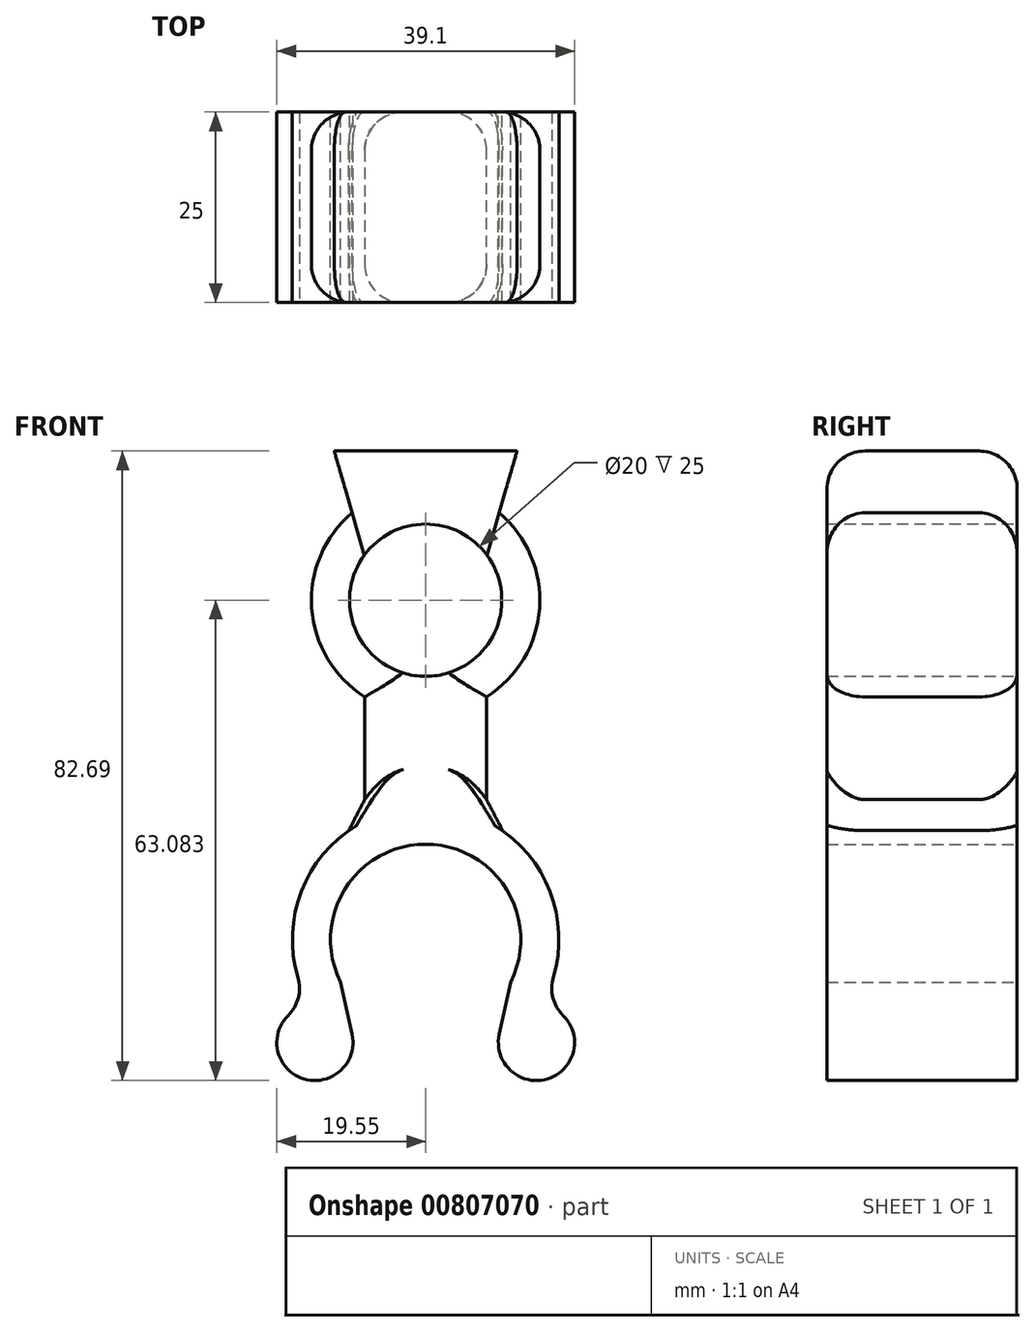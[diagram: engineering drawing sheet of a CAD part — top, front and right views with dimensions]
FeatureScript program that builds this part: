
annotation { "Feature Type Name" : "Feature", "Feature Type Description" : "" }
export const myFeature = defineFeature(function(context is Context, id is Id, definition is map)
    precondition{}
    {
        {
            var Q0;
            Q0=qCreatedBy(makeId("Front.planeOp"),FACE);
            var sketch = newSketch(context, id + "F0", { "sketchPlane" : qUnion([Q0])});
            skArc(sketch, "E0", {"start": v(15.25, -8.59) * mm, "mid": v(16.76, 5.03) * mm, "end": v(8, 15.56) * mm});
            skArc(sketch, "E1", {"start": v(11.16, -5.63) * mm, "mid": v(10.65, 6.55) * mm, "end": v(0, 12.5) * mm});
            skLineSegment(sketch, "E2", {"start": v(0, 17.5) * mm, "end": v(0, 12.5) * mm});
            skLineSegment(sketch, "E3", {"start": v(11.16, -5.63) * mm, "end": v(9.67, -12.47) * mm});
            skArc(sketch, "E4", {"start": v(9.67, -12.47) * mm, "mid": v(17.4, -17.64) * mm, "end": v(15.25, -8.59) * mm});
            skArc(sketch, "E5", {"start": v(0, 34.54) * mm, "mid": v(10, 44.54) * mm, "end": v(0, 54.54) * mm});
            skArc(sketch, "E6", {"start": v(8, 31.85) * mm, "mid": v(14.96, 43.52) * mm, "end": v(9.66, 56.02) * mm});
            skLineSegment(sketch, "E7", {"start": v(0, 59.54) * mm, "end": v(0, 69.88) * mm});
            skLineSegment(sketch, "E8", {"start": v(0, -9.02) * mm, "end": v(0, 85.69) * mm, "construction": true});
            skLineSegment(sketch, "E9", {"start": v(0, 59.54) * mm, "end": v(0, 54.54) * mm});
            skLineSegment(sketch, "E10", {"start": v(0, 29.54) * mm, "end": v(0, 34.54) * mm});
            skLineSegment(sketch, "E11", {"start": v(8, 31.85) * mm, "end": v(8, 15.56) * mm});
            skLineSegment(sketch, "E12", {"start": v(0, 29.54) * mm, "end": v(0, 17.5) * mm});
            skLineSegment(sketch, "E13", {"start": v(12, 64.15) * mm, "end": v(0, 64.15) * mm});
            skLineSegment(sketch, "E14", {"start": v(12, 64.15) * mm, "end": v(9.66, 56.02) * mm});
            skSolve(sketch);
        }
        {
            var Q0;
            Q0=qSketchRegion(id+"F0",true);
            extrude(context, id + "F1", {"entities" : qUnion([Q0]), "depth" : 25 * mm, "offsetDistance" : 25 * mm});
        }
        {
            var Q0;
            Q0=makeQuery(id+"F1.opExtrude","SWEPT_BODY",BODY,{"disambiguationData":[OSD([sQuery(id+"F0.wireOp",EDGE,"E0"),sQuery(id+"F0.wireOp",EDGE,"E1"),sQuery(id+"F0.wireOp",EDGE,"E2"),sQuery(id+"F0.wireOp",EDGE,"E3"),sQuery(id+"F0.wireOp",EDGE,"E4")])]});
            var Q1;
            Q1=makeQuery(id+"F1.opExtrude","SWEPT_BODY",BODY,{"disambiguationData":[OSD([sQuery(id+"F0.wireOp",EDGE,"E5"),sQuery(id+"F0.wireOp",EDGE,"E6"),sQuery(id+"F0.wireOp",EDGE,"ZKlF4mqJ-5DrE-eTdW-whtT-mimaQSIe7lm9"),sQuery(id+"F0.wireOp",EDGE,"B9OKSv2O-DWHs-XMQp-p7Ia-sCPH9sulsA8u"),sQuery(id+"F0.wireOp",EDGE,"7JTtOB6v-8xqh-fVU6-w0FL-nSfP0XwtOn2y"),sQuery(id+"F0.wireOp",EDGE,"698f7dfc-63ae-4ce6-86f1-02b924555ac6.filletArc"),sQuery(id+"F0.wireOp",EDGE,"46WvWRZJ-fj3N-dYTW-aIvH-BbHphLMpPgnm"),sQuery(id+"F0.wireOp",EDGE,"E9"),sQuery(id+"F0.wireOp",EDGE,"E10")])]});
            var Q2;
            Q2=qCreatedBy(makeId("Right.planeOp"),FACE);
            mirror(context, id + "F2", {"operationType" : NewBodyOperationType.ADD, "entities" : qUnion([Q0, Q1]), "mirrorPlane" : qUnion([Q2])});
        }
        {
            var Q0;
            Q0=makeQuery(id+"F2.opPattern","COPY",EDGE,{"derivedFrom":makeQuery(id+"F1.opExtrude","CAP_EDGE",EDGE,{"disambiguationData":[OSD([sQuery(id+"F0.wireOp",EDGE,"E6")])],"isStart":false}),"instanceName":"1"});
            var Q1;
            Q1=makeQuery(id+"F1.opExtrude","CAP_EDGE",EDGE,{"disambiguationData":[OSD([sQuery(id+"F0.wireOp",EDGE,"E6")])],"isStart":false});
            var Q2;
            Q2=makeQuery(id+"F1.opExtrude","CAP_EDGE",EDGE,{"disambiguationData":[OSD([sQuery(id+"F0.wireOp",EDGE,"E6")])],"isStart":true});
            var Q3;
            Q3=makeQuery(id+"F2.opPattern","COPY",EDGE,{"derivedFrom":makeQuery(id+"F1.opExtrude","CAP_EDGE",EDGE,{"disambiguationData":[OSD([sQuery(id+"F0.wireOp",EDGE,"E6")])],"isStart":true}),"instanceName":"1"});
            var Q4;
            Q4=makeQuery(id+"F1.opExtrude","CAP_EDGE",EDGE,{"disambiguationData":[OSD([sQuery(id+"F0.wireOp",EDGE,"E11")])],"isStart":true});
            var Q5;
            Q5=makeQuery(id+"F2.opPattern","COPY",EDGE,{"derivedFrom":makeQuery(id+"F1.opExtrude","CAP_EDGE",EDGE,{"disambiguationData":[OSD([sQuery(id+"F0.wireOp",EDGE,"E11")])],"isStart":true}),"instanceName":"1"});
            var Q6;
            Q6=makeQuery(id+"F2.opPattern","COPY",EDGE,{"derivedFrom":makeQuery(id+"F1.opExtrude","CAP_EDGE",EDGE,{"disambiguationData":[OSD([sQuery(id+"F0.wireOp",EDGE,"E11")])],"isStart":false}),"instanceName":"1"});
            var Q7;
            Q7=makeQuery(id+"F1.opExtrude","CAP_EDGE",EDGE,{"disambiguationData":[OSD([sQuery(id+"F0.wireOp",EDGE,"E11")])],"isStart":false});
            var Q8;
            Q8=makeQuery(id+"F2.opPattern","COPY",EDGE,{"derivedFrom":makeQuery(id+"F1.opExtrude","SWEPT_EDGE",EDGE,{"disambiguationData":[OSD([sQuery(id+"F0.wireOp",EDGE,"E0"),sQuery(id+"F0.wireOp",EDGE,"E4")])]}),"instanceName":"1"});
            var Q9;
            Q9=makeQuery(id+"F1.opExtrude","SWEPT_EDGE",EDGE,{"disambiguationData":[OSD([sQuery(id+"F0.wireOp",EDGE,"E0"),sQuery(id+"F0.wireOp",EDGE,"E4")])]});
            var Q10;
            {var subQ0=makeQuery(id+"F1.opExtrude","CAP_EDGE",EDGE,{"disambiguationData":[OSD([sQuery(id+"F0.wireOp",EDGE,"E13")])],"isStart":false});Q10=makeQuery(id+"F2.boolean.opBoolean","MERGE",EDGE,{"derivedFrom":[subQ0,makeQuery(id+"F2.opPattern","COPY",EDGE,{"derivedFrom":subQ0,"instanceName":"1"})]});}
            var Q11;
            {var subQ0=makeQuery(id+"F1.opExtrude","CAP_EDGE",EDGE,{"disambiguationData":[OSD([sQuery(id+"F0.wireOp",EDGE,"E13")])],"isStart":true});Q11=makeQuery(id+"F2.boolean.opBoolean","MERGE",EDGE,{"derivedFrom":[subQ0,makeQuery(id+"F2.opPattern","COPY",EDGE,{"derivedFrom":subQ0,"instanceName":"1"})]});}
            fillet(context, id + "F3", {"entities" : qUnion([Q0, Q1, Q2, Q3, Q4, Q5, Q6, Q7, Q8, Q9, Q10, Q11]), "radius" : 5 * mm, "tangentPropagation" : true, "allowEdgeOverflow" : false});
        }
        {
            var Q0;
            Q0=makeQuery(id+"F3.opFillet","BLEND_EDGE",EDGE,{"blendedFrom":[makeQuery(id+"F2.opPattern","COPY",EDGE,{"derivedFrom":makeQuery(id+"F1.opExtrude","CAP_EDGE",EDGE,{"disambiguationData":[OSD([sQuery(id+"F0.wireOp",EDGE,"E11")])],"isStart":false}),"instanceName":"1"}),makeQuery(id+"F2.opPattern","COPY",FACE,{"derivedFrom":makeQuery(id+"F1.opExtrude","SWEPT_FACE",FACE,{"disambiguationData":[OSD([sQuery(id+"F0.wireOp",EDGE,"E0")])]}),"instanceName":"1"})],"blendedInto":[makeQuery(id+"F2.opPattern","COPY",FACE,{"derivedFrom":makeQuery(id+"F1.opExtrude","SWEPT_FACE",FACE,{"disambiguationData":[OSD([sQuery(id+"F0.wireOp",EDGE,"E0")])]}),"instanceName":"1"})]});
            var Q1;
            Q1=makeQuery(id+"F3.opFillet","BLEND_EDGE",EDGE,{"blendedFrom":[makeQuery(id+"F1.opExtrude","CAP_EDGE",EDGE,{"disambiguationData":[OSD([sQuery(id+"F0.wireOp",EDGE,"E11")])],"isStart":false}),makeQuery(id+"F1.opExtrude","SWEPT_FACE",FACE,{"disambiguationData":[OSD([sQuery(id+"F0.wireOp",EDGE,"E0")])]})],"blendedInto":[makeQuery(id+"F1.opExtrude","SWEPT_FACE",FACE,{"disambiguationData":[OSD([sQuery(id+"F0.wireOp",EDGE,"E0")])]})]});
            chamfer(context, id + "F4", {"entities" : qUnion([Q0, Q1]), "width" : 5 * mm, "tangentPropagation" : true});
        }
    });
